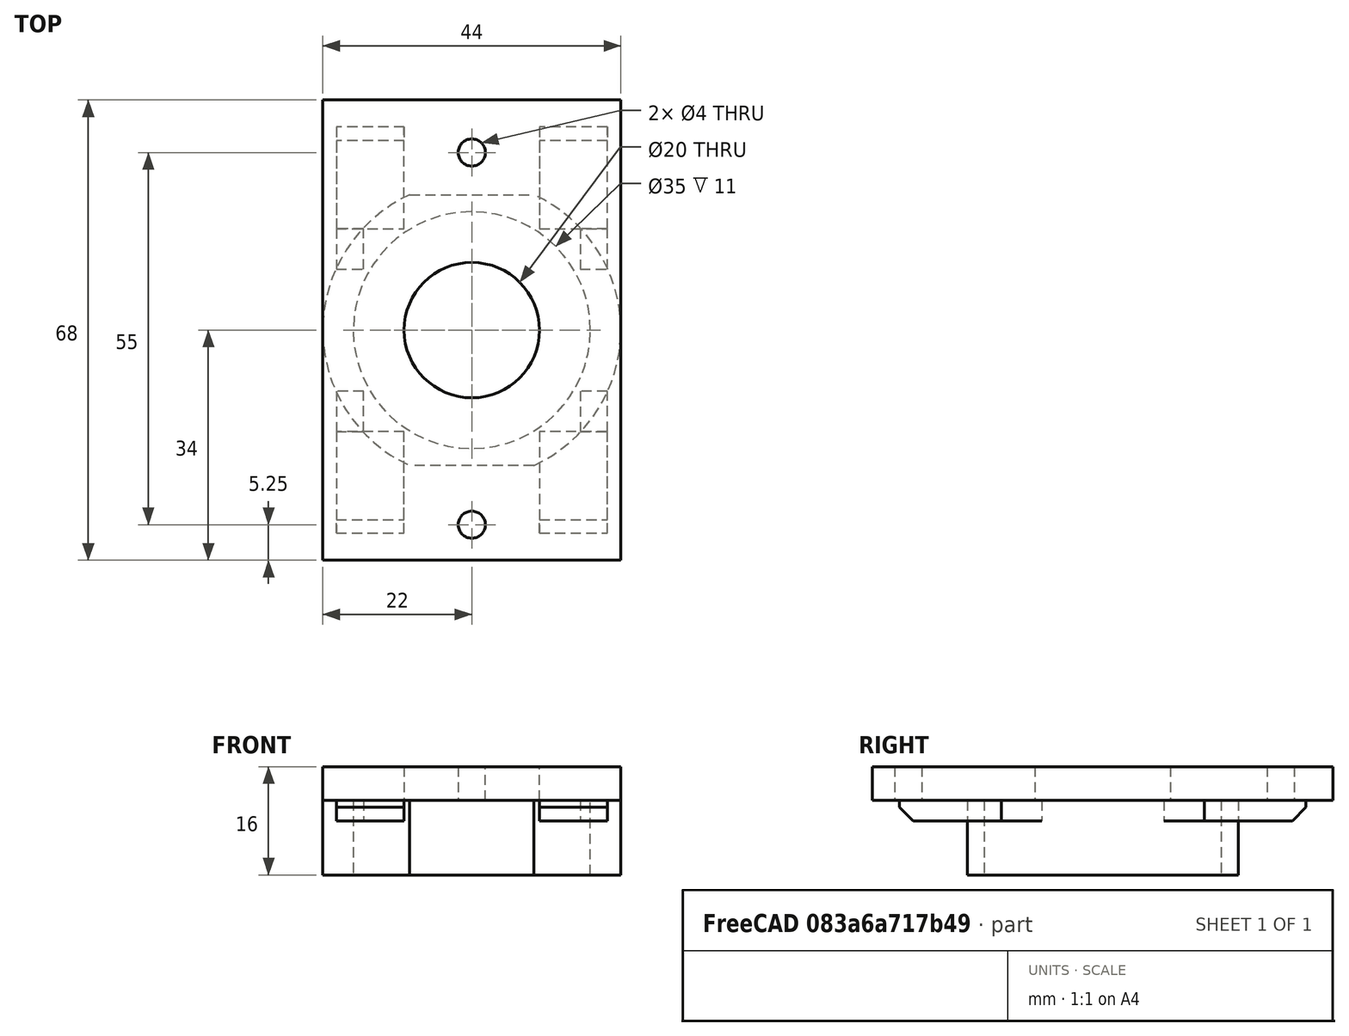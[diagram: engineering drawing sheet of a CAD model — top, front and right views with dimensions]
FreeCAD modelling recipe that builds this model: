
FCSTD DOCUMENT  (FreeCAD 0.20R29410 (Git))
Label: titan_mount_01
License: All rights reserved
LicenseURL: http://en.wikipedia.org/wiki/All_rights_reserved
objects: Part::Part2DObjectPython×24, Part::Extrusion×22, Part::Cut×9, Part::Chamfer×4, Part::MultiFuse×2
note: 61 computed .brp shape members not serialized (recipe doc carries the construction recipe); baked Part::Feature solids carry a one-line shape summary decoded from their .brp

FEATURE [Part::Part2DObjectPython] Circle  # Draft 2D object (typed FeaturePython)
  Area = 0
  FirstAngle = 0
  LastAngle = 0
  MakeFace = false
  Radius = 17.5
FEATURE [Part::Part2DObjectPython] Circle001  # Draft 2D object (typed FeaturePython)
  Area = 0
  FirstAngle = 0
  LastAngle = 0
  MakeFace = false
  Radius = 22
FEATURE [Part::Extrusion] Extrude
  Base = -> Circle
  Dir = (0,0,1)
  DirMode = 2
  FaceMakerClass = Part::FaceMakerBullseye
  LengthFwd = 11
  LengthRev = 0
  Solid = true
  Symmetric = false
FEATURE [Part::Extrusion] Extrude001
  Base = -> Circle001
  Dir = (0,0,1)
  DirMode = 2
  FaceMakerClass = Part::FaceMakerBullseye
  LengthFwd = 11
  LengthRev = 0
  Solid = true
  Symmetric = false
FEATURE [Part::Cut] Cut
  Base = -> Extrude001
  Tool = -> Extrude
FEATURE [Part::Part2DObjectPython] Rectangle  # Draft 2D object (typed FeaturePython)
  Area = 0
  ChamferSize = 0
  Columns = 1
  FilletRadius = 0
  Height = 34
  Length = 44
  MakeFace = false
  Placement = pos=(-22,-34,11) rot=(0,0,1;0rad)
  Rows = 1
FEATURE [Part::Part2DObjectPython] Rectangle001  # Draft 2D object (typed FeaturePython)
  Area = 0
  ChamferSize = 0
  Columns = 1
  FilletRadius = 0
  Height = 26.25
  Length = 20
  MakeFace = false
  Placement = pos=(-10,-26.25,11) rot=(0,0,1;0rad)
  Rows = 1
FEATURE [Part::Part2DObjectPython] Rectangle002  # Draft 2D object (typed FeaturePython)
  Area = 0
  ChamferSize = 0
  Columns = 1
  FilletRadius = 0
  Height = 26.25
  Length = 20
  MakeFace = false
  Placement = pos=(-10,0,11) rot=(0,0,1;0rad)
  Rows = 1
FEATURE [Part::Part2DObjectPython] Rectangle003  # Draft 2D object (typed FeaturePython)
  Area = 0
  ChamferSize = 0
  Columns = 1
  FilletRadius = 0
  Height = 34
  Length = 44
  MakeFace = false
  Placement = pos=(-22,0,11) rot=(0,0,1;0rad)
  Rows = 1
FEATURE [Part::Part2DObjectPython] Rectangle004  # Draft 2D object (typed FeaturePython)
  Area = 0
  ChamferSize = 0
  Columns = 1
  FilletRadius = 0
  Height = 6.25
  Length = 20
  MakeFace = false
  Placement = pos=(-10,-26.25,11) rot=(0,0,1;0rad)
  Rows = 1
FEATURE [Part::Part2DObjectPython] Rectangle005  # Draft 2D object (typed FeaturePython)
  Area = 0
  ChamferSize = 0
  Columns = 1
  FilletRadius = 0
  Height = 6.25
  Length = 20
  MakeFace = false
  Placement = pos=(-10,20,11) rot=(0,0,1;0rad)
  Rows = 1
FEATURE [Part::Extrusion] Extrude002
  Base = -> Rectangle004
  Dir = (0,0,1)
  DirMode = 2
  FaceMakerClass = Part::FaceMakerBullseye
  LengthFwd = -11
  LengthRev = 0
  Solid = true
  Symmetric = false
FEATURE [Part::Extrusion] Extrude003
  Base = -> Rectangle005
  Dir = (0,0,1)
  DirMode = 2
  FaceMakerClass = Part::FaceMakerBullseye
  LengthFwd = -11
  LengthRev = 0
  Solid = true
  Symmetric = false
FEATURE [Part::Cut] Cut001
  Base = -> Cut
  Tool = -> Extrude002
FEATURE [Part::Cut] Cut002
  Base = -> Cut001
  Tool = -> Extrude003
FEATURE [Part::Extrusion] Extrude004
  Base = -> Rectangle
  Dir = (0,0,1)
  DirMode = 2
  FaceMakerClass = Part::FaceMakerBullseye
  LengthFwd = 5
  LengthRev = 0
  Solid = true
  Symmetric = false
FEATURE [Part::Extrusion] Extrude005
  Base = -> Rectangle003
  Dir = (0,0,1)
  DirMode = 2
  FaceMakerClass = Part::FaceMakerBullseye
  LengthFwd = 5
  LengthRev = 0
  Solid = true
  Symmetric = false
FEATURE [Part::Part2DObjectPython] Circle002  # Draft 2D object (typed FeaturePython)
  Area = 0
  FirstAngle = 0
  LastAngle = 0
  MakeFace = false
  Placement = pos=(0,0,11) rot=(0,0,1;0rad)
  Radius = 10
FEATURE [Part::Extrusion] Extrude006
  Base = -> Circle002
  Dir = (0,0,1)
  DirMode = 2
  FaceMakerClass = Part::FaceMakerBullseye
  LengthFwd = 5
  LengthRev = 0
  Solid = true
  Symmetric = false
FEATURE [Part::MultiFuse] Fusion
  Shapes = -> [Extrude005,Extrude004]
FEATURE [Part::Cut] Cut003
  Base = -> Fusion
  Tool = -> Extrude006
FEATURE [Part::Part2DObjectPython] Rectangle006  # Draft 2D object (typed FeaturePython)
  Area = 0
  ChamferSize = 0
  Columns = 1
  FilletRadius = 0
  Height = 15
  Length = 10
  MakeFace = false
  Placement = pos=(10,15,11) rot=(0,0,1;0rad)
  Rows = 1
FEATURE [Part::Part2DObjectPython] Rectangle007  # Draft 2D object (typed FeaturePython)
  Area = 0
  ChamferSize = 0
  Columns = 1
  FilletRadius = 0
  Height = 15
  Length = 10
  MakeFace = false
  Placement = pos=(10,-30,11) rot=(0,0,1;0rad)
  Rows = 1
FEATURE [Part::Part2DObjectPython] Rectangle008  # Draft 2D object (typed FeaturePython)
  Area = 0
  ChamferSize = 0
  Columns = 1
  FilletRadius = 0
  Height = 15
  Length = 10
  MakeFace = false
  Placement = pos=(-20,15,11) rot=(0,0,1;0rad)
  Rows = 1
FEATURE [Part::Part2DObjectPython] Rectangle009  # Draft 2D object (typed FeaturePython)
  Area = 0
  ChamferSize = 0
  Columns = 1
  FilletRadius = 0
  Height = 15
  Length = 10
  MakeFace = false
  Placement = pos=(-20,-30,11) rot=(0,0,1;0rad)
  Rows = 1
FEATURE [Part::Part2DObjectPython] Rectangle010  # Draft 2D object (typed FeaturePython)
  Area = 0
  ChamferSize = 0
  Columns = 1
  FilletRadius = 0
  Height = 6
  Length = 4
  MakeFace = false
  Placement = pos=(16,-15,11) rot=(0,0,1;0rad)
  Rows = 1
FEATURE [Part::Part2DObjectPython] Rectangle011  # Draft 2D object (typed FeaturePython)
  Area = 0
  ChamferSize = 0
  Columns = 1
  FilletRadius = 0
  Height = 6
  Length = 4
  MakeFace = false
  Placement = pos=(16,9,11) rot=(0,0,1;0rad)
  Rows = 1
FEATURE [Part::Part2DObjectPython] Rectangle012  # Draft 2D object (typed FeaturePython)
  Area = 0
  ChamferSize = 0
  Columns = 1
  FilletRadius = 0
  Height = 6
  Length = 4
  MakeFace = false
  Placement = pos=(-20,9,11) rot=(0,0,1;0rad)
  Rows = 1
FEATURE [Part::Part2DObjectPython] Rectangle013  # Draft 2D object (typed FeaturePython)
  Area = 0
  ChamferSize = 0
  Columns = 1
  FilletRadius = 0
  Height = 6
  Length = 4
  MakeFace = false
  Placement = pos=(-20,-15,11) rot=(0,0,1;0rad)
  Rows = 1
FEATURE [Part::Extrusion] Extrude007
  Base = -> Rectangle006
  Dir = (0,0,1)
  DirMode = 2
  FaceMakerClass = Part::FaceMakerBullseye
  LengthFwd = -3
  LengthRev = 0
  Solid = true
  Symmetric = false
FEATURE [Part::Extrusion] Extrude008
  Base = -> Rectangle008
  Dir = (0,0,1)
  DirMode = 2
  FaceMakerClass = Part::FaceMakerBullseye
  LengthFwd = -3
  LengthRev = 0
  Solid = true
  Symmetric = false
FEATURE [Part::Extrusion] Extrude009
  Base = -> Rectangle007
  Dir = (0,0,1)
  DirMode = 2
  FaceMakerClass = Part::FaceMakerBullseye
  LengthFwd = -3
  LengthRev = 0
  Solid = true
  Symmetric = false
FEATURE [Part::Extrusion] Extrude010
  Base = -> Rectangle009
  Dir = (0,0,1)
  DirMode = 2
  FaceMakerClass = Part::FaceMakerBullseye
  LengthFwd = -3
  LengthRev = 0
  Solid = true
  Symmetric = false
FEATURE [Part::Extrusion] Extrude011
  Base = -> Rectangle010
  Dir = (0,0,1)
  DirMode = 2
  FaceMakerClass = Part::FaceMakerBullseye
  LengthFwd = -3
  LengthRev = 0
  Solid = true
  Symmetric = false
FEATURE [Part::Extrusion] Extrude012
  Base = -> Rectangle011
  Dir = (0,0,1)
  DirMode = 2
  FaceMakerClass = Part::FaceMakerBullseye
  LengthFwd = -3
  LengthRev = 0
  Solid = true
  Symmetric = false
FEATURE [Part::Extrusion] Extrude013
  Base = -> Rectangle012
  Dir = (0,0,1)
  DirMode = 2
  FaceMakerClass = Part::FaceMakerBullseye
  LengthFwd = -3
  LengthRev = 0
  Solid = true
  Symmetric = false
FEATURE [Part::Extrusion] Extrude014
  Base = -> Rectangle013
  Dir = (0,0,1)
  DirMode = 2
  FaceMakerClass = Part::FaceMakerBullseye
  LengthFwd = -3
  LengthRev = 0
  Solid = true
  Symmetric = false
FEATURE [Part::Chamfer] Chamfer
  Base = -> Extrude007
  Edges = 1 edges r=2: [Edge10]
FEATURE [Part::Chamfer] Chamfer001
  Base = -> Extrude008
  Edges = 1 edges r=2: [Edge10]
FEATURE [Part::Chamfer] Chamfer002
  Base = -> Extrude009
  Edges = 1 edges r=2: [Edge4]
FEATURE [Part::Chamfer] Chamfer003
  Base = -> Extrude010
  Edges = 1 edges r=2: [Edge4]
FEATURE [Part::Part2DObjectPython] Circle003  # Draft 2D object (typed FeaturePython)
  Area = 0
  FirstAngle = 0
  LastAngle = 0
  MakeFace = false
  Placement = pos=(0,-26.25,11) rot=(0,0,1;0rad)
  Radius = 2
FEATURE [Part::Part2DObjectPython] Circle004  # Draft 2D object (typed FeaturePython)
  Area = 0
  FirstAngle = 0
  LastAngle = 0
  MakeFace = false
  Placement = pos=(0,26.25,11) rot=(0,0,1;0rad)
  Radius = 2
FEATURE [Part::Extrusion] Extrude015
  Base = -> Circle004
  Dir = (0,0,1)
  DirMode = 2
  FaceMakerClass = Part::FaceMakerBullseye
  LengthFwd = 5
  LengthRev = 0
  Solid = true
  Symmetric = false
FEATURE [Part::Extrusion] Extrude016
  Base = -> Circle003
  Dir = (0,0,1)
  DirMode = 2
  FaceMakerClass = Part::FaceMakerBullseye
  LengthFwd = 5
  LengthRev = 0
  Solid = true
  Symmetric = false
FEATURE [Part::Cut] Cut004
  Base = -> Cut003
  Tool = -> Extrude015
FEATURE [Part::Cut] Cut005
  Base = -> Cut004
  Tool = -> Extrude016
FEATURE [Part::Part2DObjectPython] Circle005  # Draft 2D object (typed FeaturePython)
  Area = 0
  FirstAngle = 0
  LastAngle = 0
  MakeFace = false
  Placement = pos=(0,0,11) rot=(0,0,1;0rad)
  Radius = 10
FEATURE [Part::Part2DObjectPython] Circle006  # Draft 2D object (typed FeaturePython)
  Area = 0
  FirstAngle = 0
  LastAngle = 0
  MakeFace = false
  Placement = pos=(0,26.25,11) rot=(0,0,1;0rad)
  Radius = 2
FEATURE [Part::Extrusion] Extrude019
  Base = -> Circle005
  Dir = (0,0,1)
  DirMode = 2
  FaceMakerClass = Part::FaceMakerBullseye
  LengthFwd = 5
  LengthRev = 0
  Solid = true
  Symmetric = false
FEATURE [Part::Extrusion] Extrude020
  Base = -> Circle006
  Dir = (0,0,1)
  DirMode = 2
  FaceMakerClass = Part::FaceMakerBullseye
  LengthFwd = 5
  LengthRev = 0
  Solid = true
  Symmetric = false
FEATURE [Part::Part2DObjectPython] Rectangle014  # Draft 2D object (typed FeaturePython)
  Area = 0
  ChamferSize = 0
  Columns = 1
  FilletRadius = 0
  Height = 34
  Length = 44
  MakeFace = false
  Placement = pos=(-22,-34,11) rot=(0,0,1;0rad)
  Rows = 1
FEATURE [Part::Extrusion] Extrude017
  Base = -> Rectangle014
  Dir = (0,0,1)
  DirMode = 2
  FaceMakerClass = Part::FaceMakerBullseye
  LengthFwd = 5
  LengthRev = 0
  Solid = true
  Symmetric = false
FEATURE [Part::Part2DObjectPython] Rectangle015  # Draft 2D object (typed FeaturePython)
  Area = 0
  ChamferSize = 0
  Columns = 1
  FilletRadius = 0
  Height = 34
  Length = 44
  MakeFace = false
  Placement = pos=(-22,0,11) rot=(0,0,1;0rad)
  Rows = 1
FEATURE [Part::Extrusion] Extrude018
  Base = -> Rectangle015
  Dir = (0,0,1)
  DirMode = 2
  FaceMakerClass = Part::FaceMakerBullseye
  LengthFwd = 5
  LengthRev = 0
  Solid = true
  Symmetric = false
FEATURE [Part::MultiFuse] Fusion001
  Shapes = -> [Extrude018,Extrude017]
FEATURE [Part::Cut] Cut006
  Base = -> Fusion001
  Tool = -> Extrude019
FEATURE [Part::Cut] Cut007
  Base = -> Cut006
  Tool = -> Extrude020
FEATURE [Part::Part2DObjectPython] Circle007  # Draft 2D object (typed FeaturePython)
  Area = 0
  FirstAngle = 0
  LastAngle = 0
  MakeFace = false
  Placement = pos=(0,-26.25,11) rot=(0,0,1;0rad)
  Radius = 2
FEATURE [Part::Extrusion] Extrude021
  Base = -> Circle007
  Dir = (0,0,1)
  DirMode = 2
  FaceMakerClass = Part::FaceMakerBullseye
  LengthFwd = 5
  LengthRev = 0
  Placement = pos=(0,-2.5,0) rot=(0,0,1;0rad)
  Solid = true
  Symmetric = false
FEATURE [Part::Cut] Cut008
  Base = -> Cut007
  Tool = -> Extrude021
